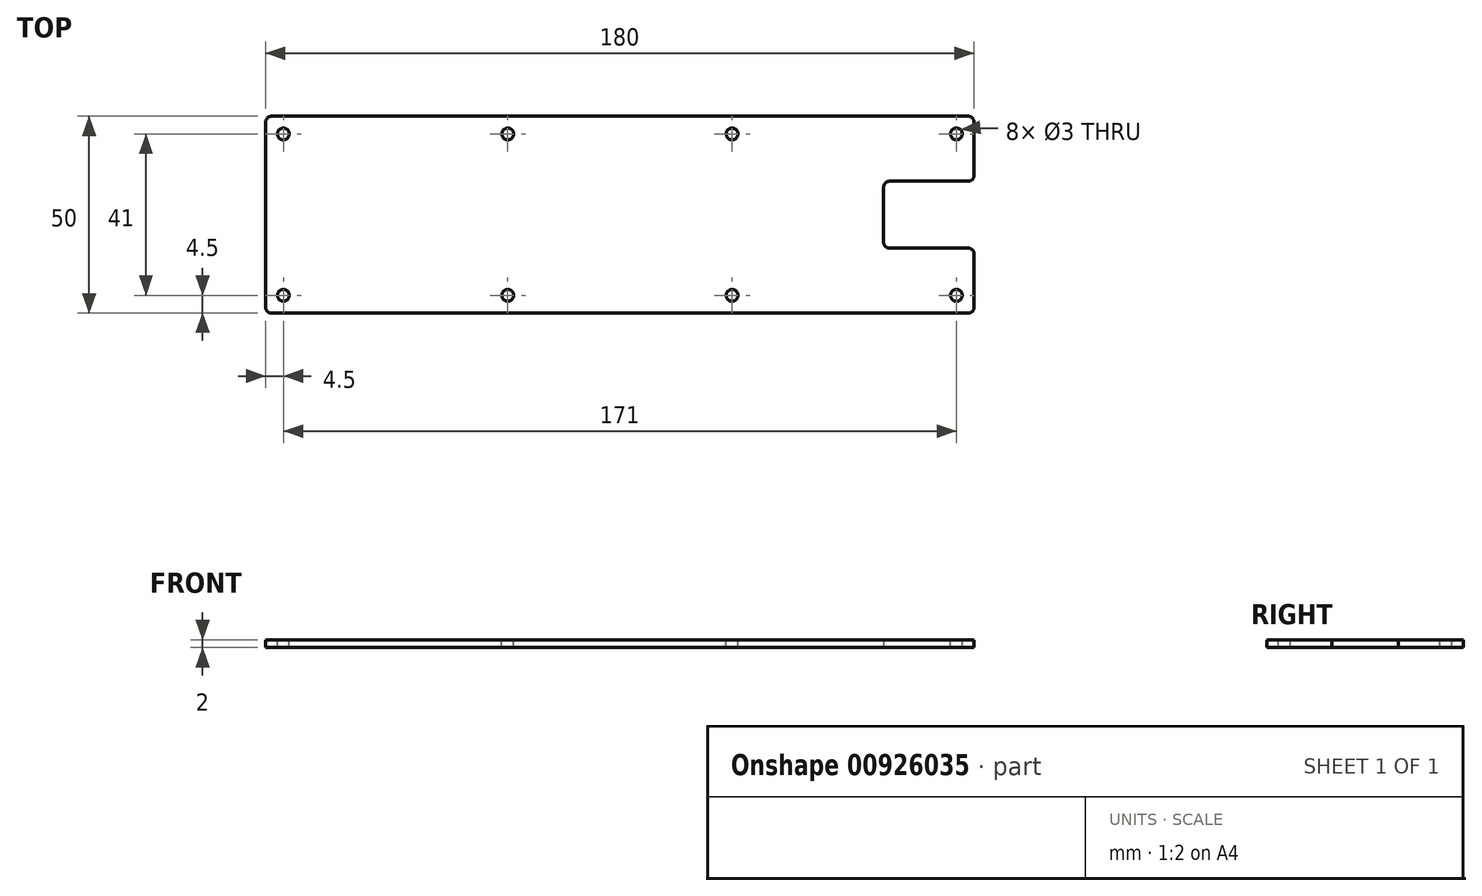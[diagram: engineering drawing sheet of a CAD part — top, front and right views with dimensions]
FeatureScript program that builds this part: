
annotation { "Feature Type Name" : "Feature", "Feature Type Description" : "" }
export const myFeature = defineFeature(function(context is Context, id is Id, definition is map)
    precondition{}
    {
        {
            var Q0;
            Q0=qCreatedBy(makeId("Top.planeOp"),FACE);
            var sketch = newSketch(context, id + "F0", { "sketchPlane" : qUnion([Q0])});
            skLineSegment(sketch, "E0", {"start": v(-88.5, 25) * mm, "end": v(88.5, 25) * mm});
            skLineSegment(sketch, "E1", {"start": v(90, 23.5) * mm, "end": v(90, 10) * mm});
            skLineSegment(sketch, "E2", {"start": v(88.5, 8.5) * mm, "end": v(68.5, 8.5) * mm});
            skLineSegment(sketch, "E3", {"start": v(67, 7) * mm, "end": v(67, -7) * mm});
            skLineSegment(sketch, "E4", {"start": v(68.5, -8.5) * mm, "end": v(88.5, -8.5) * mm});
            skLineSegment(sketch, "E5", {"start": v(90, -10) * mm, "end": v(90, -23.5) * mm});
            skLineSegment(sketch, "E6", {"start": v(88.5, -25) * mm, "end": v(-88.5, -25) * mm});
            skLineSegment(sketch, "E7", {"start": v(-90, -23.5) * mm, "end": v(-90, 23.5) * mm});
            skArc(sketch, "E8.filletArc", {"start": v(-88.5, 25) * mm, "mid": v(-89.56, 24.56) * mm, "end": v(-90, 23.5) * mm});
            skArc(sketch, "E9.filletArc", {"start": v(-90, -23.5) * mm, "mid": v(-89.56, -24.56) * mm, "end": v(-88.5, -25) * mm});
            skArc(sketch, "E10.filletArc", {"start": v(88.5, -25) * mm, "mid": v(89.56, -24.56) * mm, "end": v(90, -23.5) * mm});
            skArc(sketch, "E11.filletArc", {"start": v(90, -10) * mm, "mid": v(89.56, -8.94) * mm, "end": v(88.5, -8.5) * mm});
            skArc(sketch, "E12.filletArc", {"start": v(67, -7) * mm, "mid": v(67.44, -8.06) * mm, "end": v(68.5, -8.5) * mm});
            skArc(sketch, "E13.filletArc", {"start": v(68.5, 8.5) * mm, "mid": v(67.44, 8.06) * mm, "end": v(67, 7) * mm});
            skArc(sketch, "E14.filletArc", {"start": v(88.5, 8.5) * mm, "mid": v(89.56, 8.94) * mm, "end": v(90, 10) * mm});
            skArc(sketch, "E15.filletArc", {"start": v(90, 23.5) * mm, "mid": v(89.56, 24.56) * mm, "end": v(88.5, 25) * mm});
            skSolve(sketch);
        }
        {
            var Q0;
            Q0 = qSketchRegion(id + "F0", true);
            extrude(context, id + "F1", {"entities" : qUnion([Q0]), "depth" : 2 * mm, "offsetDistance" : 25 * mm});
        }
        {
            var Q0;
            Q0=makeQuery(id+"F1.opExtrude","CAP_FACE",FACE,{"disambiguationData":[OSD([sQuery(id+"F0.wireOp",EDGE,"E0"),sQuery(id+"F0.wireOp",EDGE,"E1"),sQuery(id+"F0.wireOp",EDGE,"E2"),sQuery(id+"F0.wireOp",EDGE,"E3"),sQuery(id+"F0.wireOp",EDGE,"E4"),sQuery(id+"F0.wireOp",EDGE,"E5"),sQuery(id+"F0.wireOp",EDGE,"E6"),sQuery(id+"F0.wireOp",EDGE,"E7"),sQuery(id+"F0.wireOp",EDGE,"E8.filletArc"),sQuery(id+"F0.wireOp",EDGE,"E9.filletArc"),sQuery(id+"F0.wireOp",EDGE,"E10.filletArc"),sQuery(id+"F0.wireOp",EDGE,"E11.filletArc"),sQuery(id+"F0.wireOp",EDGE,"E12.filletArc"),sQuery(id+"F0.wireOp",EDGE,"E13.filletArc"),sQuery(id+"F0.wireOp",EDGE,"E14.filletArc"),sQuery(id+"F0.wireOp",EDGE,"E15.filletArc")])],"isStart":false});
            var sketch = newSketch(context, id + "F2", { "sketchPlane" : qUnion([Q0])});
            skCircle(sketch, "E16", {"center": v(-85.5, 20.5) * mm, "radius": 1.5 * mm});
            skCircle(sketch, "E17", {"center": v(-85.5, -20.5) * mm, "radius": 1.5 * mm});
            skCircle(sketch, "E18.1.0.0", {"center": v(-28.5, -20.5) * mm, "radius": 1.5 * mm});
            skCircle(sketch, "E18.1.0.1", {"center": v(-28.5, 20.5) * mm, "radius": 1.5 * mm});
            skCircle(sketch, "E18.2.0.0", {"center": v(28.5, -20.5) * mm, "radius": 1.5 * mm});
            skCircle(sketch, "E18.2.0.1", {"center": v(28.5, 20.5) * mm, "radius": 1.5 * mm});
            skLineSegment(sketch, "E18.direction1", {"start": v(-85.5, -20.5) * mm, "end": v(-28.5, -20.5) * mm, "construction": true});
            skCircle(sketch, "E19.0.3.0", {"center": v(85.5, -20.5) * mm, "radius": 1.5 * mm});
            skCircle(sketch, "E19.2.3.0", {"center": v(85.5, 20.5) * mm, "radius": 1.5 * mm});
            skSolve(sketch);
        }
        {
            var Q0;
            Q0 = qSketchRegion(id + "F2", true);
            extrude(context, id + "F3", {"entities" : qUnion([Q0]), "operationType" : NewBodyOperationType.REMOVE, "endBound" : BoundingType.THROUGH_ALL, "oppositeDirection" : true, "depth" : 25 * mm, "offsetDistance" : 25 * mm});
        }
    });
